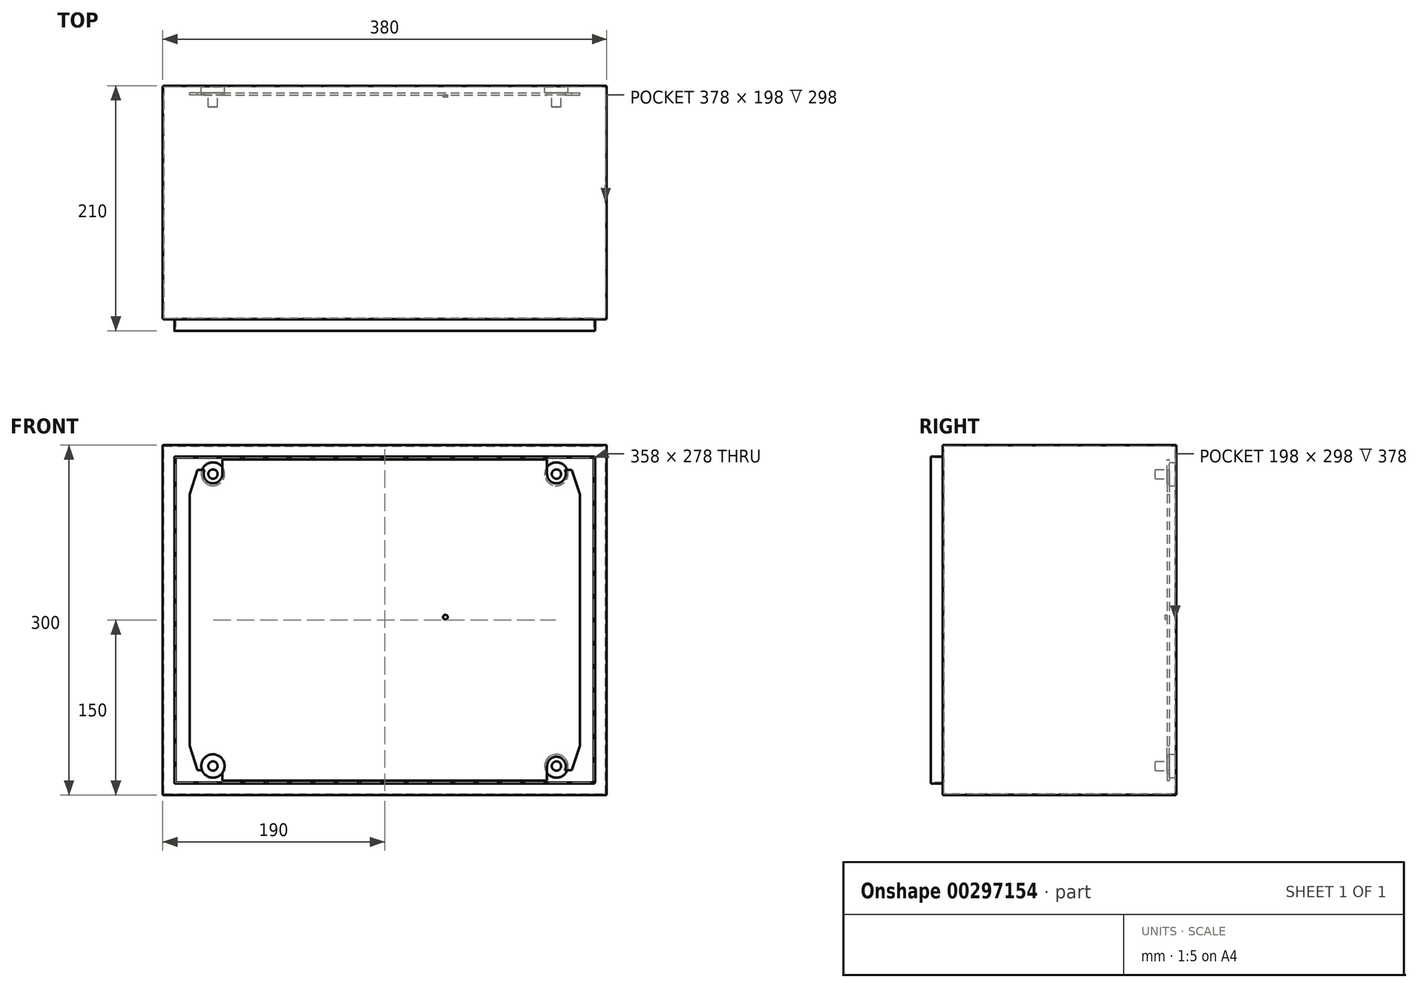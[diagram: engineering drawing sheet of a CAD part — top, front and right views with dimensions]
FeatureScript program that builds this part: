
annotation { "Feature Type Name" : "Feature", "Feature Type Description" : "" }
export const myFeature = defineFeature(function(context is Context, id is Id, definition is map)
    precondition{}
    {
        {
            var Q0;
            Q0=qCreatedBy(makeId("Front.planeOp"),FACE);
            var sketch = newSketch(context, id + "F0", { "sketchPlane" : qUnion([Q0])});
            skLineSegment(sketch, "E0.bottom", {"start": v(190, 150) * mm, "end": v(-190, 150) * mm});
            skLineSegment(sketch, "E0.top", {"start": v(190, -150) * mm, "end": v(-190, -150) * mm});
            skLineSegment(sketch, "E0.left", {"start": v(190, 150) * mm, "end": v(190, -150) * mm});
            skLineSegment(sketch, "E0.right", {"start": v(-190, 150) * mm, "end": v(-190, -150) * mm});
            skPoint(sketch, "E0.middle", {"position": v(0, 0) * mm});
            skSolve(sketch);
        }
        {
            var Q0;
            Q0=makeQuery(id+"F0.imprint","IMPRINT",FACE,{"disambiguationData":[TD([[makeQuery(id+"F0.imprint","IMPRINT",EDGE,{"derivedFrom":sQuery(id+"F0.wireOp",EDGE,"E0.bottom")}),1.0]])]});
            extrude(context, id + "F1", {"entities" : qUnion([Q0]), "depth" : 200 * mm});
        }
        {
            var Q0;
            Q0=makeQuery(id+"F1.opExtrude","CAP_FACE",FACE,{"disambiguationData":[OSD([sQuery(id+"F0.wireOp",EDGE,"E0.bottom"),sQuery(id+"F0.wireOp",EDGE,"E0.top"),sQuery(id+"F0.wireOp",EDGE,"E0.left"),sQuery(id+"F0.wireOp",EDGE,"E0.right")])],"isStart":false});
            var sketch = newSketch(context, id + "F2", { "sketchPlane" : qUnion([Q0])});
            skLineSegment(sketch, "E1.0", {"start": v(190, 150) * mm, "end": v(-190, 150) * mm});
            skLineSegment(sketch, "E1.1", {"start": v(190, 150) * mm, "end": v(190, -150) * mm});
            skLineSegment(sketch, "E1.2", {"start": v(190, -150) * mm, "end": v(-190, -150) * mm});
            skLineSegment(sketch, "E1.3", {"start": v(-190, 150) * mm, "end": v(-190, -150) * mm});
            skLineSegment(sketch, "E2.0", {"start": v(180, 140) * mm, "end": v(-180, 140) * mm});
            skLineSegment(sketch, "E2.1", {"start": v(180, 140) * mm, "end": v(180, -140) * mm});
            skLineSegment(sketch, "E2.2", {"start": v(180, -140) * mm, "end": v(-180, -140) * mm});
            skLineSegment(sketch, "E2.3", {"start": v(-180, 140) * mm, "end": v(-180, -140) * mm});
            skSolve(sketch);
        }
        {
            var Q0;
            Q0=makeQuery(id+"F2.imprint","IMPRINT",FACE,{"disambiguationData":[TD([[makeQuery(id+"F2.imprint","IMPRINT",EDGE,{"derivedFrom":sQuery(id+"F2.wireOp",EDGE,"E2.0")}),1.0]])]});
            extrude(context, id + "F3", {"entities" : qUnion([Q0]), "operationType" : NewBodyOperationType.ADD, "depth" : 10 * mm});
        }
        {
            var Q0;
            Q0=makeQuery(id+"F1.opExtrude","SWEPT_EDGE",EDGE,{"disambiguationData":[OSD([sQuery(id+"F0.wireOp",EDGE,"E0.bottom"),sQuery(id+"F0.wireOp",EDGE,"E0.left")])]});
            var Q1;
            Q1=makeQuery(id+"F1.opExtrude","CAP_EDGE",EDGE,{"disambiguationData":[OSD([sQuery(id+"F0.wireOp",EDGE,"E0.left")])],"isStart":false});
            var Q2;
            Q2=makeQuery(id+"F1.opExtrude","SWEPT_EDGE",EDGE,{"disambiguationData":[OSD([sQuery(id+"F0.wireOp",EDGE,"E0.top"),sQuery(id+"F0.wireOp",EDGE,"E0.left")])]});
            var Q3;
            Q3=makeQuery(id+"F1.opExtrude","CAP_EDGE",EDGE,{"disambiguationData":[OSD([sQuery(id+"F0.wireOp",EDGE,"E0.left")])],"isStart":true});
            var Q4;
            Q4=makeQuery(id+"F1.opExtrude","CAP_EDGE",EDGE,{"disambiguationData":[OSD([sQuery(id+"F0.wireOp",EDGE,"E0.bottom")])],"isStart":false});
            var Q5;
            Q5=makeQuery(id+"F1.opExtrude","SWEPT_EDGE",EDGE,{"disambiguationData":[OSD([sQuery(id+"F0.wireOp",EDGE,"E0.bottom"),sQuery(id+"F0.wireOp",EDGE,"E0.right")])]});
            var Q6;
            Q6=makeQuery(id+"F1.opExtrude","SWEPT_EDGE",EDGE,{"disambiguationData":[OSD([sQuery(id+"F0.wireOp",EDGE,"E0.top"),sQuery(id+"F0.wireOp",EDGE,"E0.right")])]});
            var Q7;
            Q7=makeQuery(id+"F1.opExtrude","CAP_EDGE",EDGE,{"disambiguationData":[OSD([sQuery(id+"F0.wireOp",EDGE,"E0.right")])],"isStart":false});
            var Q8;
            Q8=makeQuery(id+"F1.opExtrude","CAP_EDGE",EDGE,{"disambiguationData":[OSD([sQuery(id+"F0.wireOp",EDGE,"E0.right")])],"isStart":true});
            var Q9;
            Q9=makeQuery(id+"F1.opExtrude","CAP_EDGE",EDGE,{"disambiguationData":[OSD([sQuery(id+"F0.wireOp",EDGE,"E0.bottom")])],"isStart":true});
            var Q10;
            Q10=makeQuery(id+"F1.opExtrude","CAP_EDGE",EDGE,{"disambiguationData":[OSD([sQuery(id+"F0.wireOp",EDGE,"E0.top")])],"isStart":false});
            var Q11;
            Q11=makeQuery(id+"F1.opExtrude","CAP_EDGE",EDGE,{"disambiguationData":[OSD([sQuery(id+"F0.wireOp",EDGE,"E0.top")])],"isStart":true});
            var Q12;
            Q12=makeQuery(id+"F3.opExtrude","SWEPT_EDGE",EDGE,{"disambiguationData":[OSD([sQuery(id+"F2.wireOp",EDGE,"E2.0"),sQuery(id+"F2.wireOp",EDGE,"E2.1")])]});
            var Q13;
            Q13=makeQuery(id+"F3.opExtrude","SWEPT_EDGE",EDGE,{"disambiguationData":[OSD([sQuery(id+"F2.wireOp",EDGE,"E2.0"),sQuery(id+"F2.wireOp",EDGE,"E2.3")])]});
            var Q14;
            Q14=makeQuery(id+"F3.opExtrude","SWEPT_EDGE",EDGE,{"disambiguationData":[OSD([sQuery(id+"F2.wireOp",EDGE,"E2.1"),sQuery(id+"F2.wireOp",EDGE,"E2.2")])]});
            var Q15;
            Q15=makeQuery(id+"F3.opExtrude","SWEPT_EDGE",EDGE,{"disambiguationData":[OSD([sQuery(id+"F2.wireOp",EDGE,"E2.2"),sQuery(id+"F2.wireOp",EDGE,"E2.3")])]});
            fillet(context, id + "F4", {"entities" : qUnion([Q0, Q1, Q2, Q3, Q4, Q5, Q6, Q7, Q8, Q9, Q10, Q11, Q12, Q13, Q14, Q15]), "radius" : 1 * mm, "tangentPropagation" : true, "allowEdgeOverflow" : false});
        }
        {
            var Q0;
            Q0=makeQuery(id+"F3.opExtrude","CAP_FACE",FACE,{"disambiguationData":[OSD([sQuery(id+"F2.wireOp",EDGE,"E2.0"),sQuery(id+"F2.wireOp",EDGE,"E2.1"),sQuery(id+"F2.wireOp",EDGE,"E2.2"),sQuery(id+"F2.wireOp",EDGE,"E2.3")])],"isStart":false});
            shell(context, id + "F5", {"entities" : qUnion([Q0]), "thickness" : 1 * mm});
        }
        {
            var Q0;
            {var subQ0=sQuery(id+"F0.wireOp",EDGE,"E0.right");var subQ1=sQuery(id+"F0.wireOp",EDGE,"E0.left");var subQ2=sQuery(id+"F0.wireOp",EDGE,"E0.top");var subQ3=sQuery(id+"F0.wireOp",EDGE,"E0.bottom");Q0=makeQuery(id+"F5.opShell","OFFSET_FACE",FACE,{"disambiguationData":[OSD([subQ3,subQ2,subQ1,subQ0]),TDD([makeQuery(id+"F1.opExtrude","CAP_FACE",FACE,{"disambiguationData":[OSD([subQ3,subQ2,subQ1,subQ0])],"isStart":true})])]});}
            var sketch = newSketch(context, id + "F6", { "sketchPlane" : qUnion([Q0])});
            skLineSegment(sketch, "E3.bottom", {"start": v(147, -125) * mm, "end": v(-147, -125) * mm, "construction": true});
            skLineSegment(sketch, "E3.top", {"start": v(147, 125) * mm, "end": v(-147, 125) * mm, "construction": true});
            skLineSegment(sketch, "E3.left", {"start": v(147, -125) * mm, "end": v(147, 125) * mm, "construction": true});
            skLineSegment(sketch, "E3.right", {"start": v(-147, -125) * mm, "end": v(-147, 125) * mm, "construction": true});
            skPoint(sketch, "E3.middle", {"position": v(0, 0) * mm});
            skCircle(sketch, "E4", {"center": v(-147, 125) * mm, "radius": 10 * mm});
            skCircle(sketch, "E5.0.1.0", {"center": v(-147, -125) * mm, "radius": 10 * mm});
            skLineSegment(sketch, "E5.direction1", {"start": v(-147, 125) * mm, "end": v(147, 125) * mm, "construction": true});
            skLineSegment(sketch, "E5.direction2", {"start": v(-147, 125) * mm, "end": v(-147, -125) * mm, "construction": true});
            skCircle(sketch, "E6.0.1.0", {"center": v(147, 125) * mm, "radius": 10 * mm});
            skCircle(sketch, "E6.0.1.1", {"center": v(147, -125) * mm, "radius": 10 * mm});
            skCircle(sketch, "E7", {"center": v(-147, 125) * mm, "radius": 4 * mm});
            skCircle(sketch, "E8.0.1.0", {"center": v(-147, -125) * mm, "radius": 4 * mm});
            skCircle(sketch, "E8.1.0.0", {"center": v(147, 125) * mm, "radius": 4 * mm});
            skCircle(sketch, "E8.1.1.0", {"center": v(147, -125) * mm, "radius": 4 * mm});
            skSolve(sketch);
        }
        {
            var Q0;
            Q0=makeQuery(id+"F6.imprint","IMPRINT",FACE,{"disambiguationData":[TD([[makeQuery(id+"F6.imprint","IMPRINT",EDGE,{"derivedFrom":sQuery(id+"F6.wireOp",EDGE,"E5.0.1.0")}),1.0]])]});
            var Q1;
            Q1=makeQuery(id+"F6.imprint","IMPRINT",FACE,{"disambiguationData":[TD([[makeQuery(id+"F6.imprint","IMPRINT",EDGE,{"derivedFrom":sQuery(id+"F6.wireOp",EDGE,"E8.0.1.0")}),1.0]])]});
            var Q2;
            Q2=makeQuery(id+"F6.imprint","IMPRINT",FACE,{"disambiguationData":[TD([[makeQuery(id+"F6.imprint","IMPRINT",EDGE,{"derivedFrom":sQuery(id+"F6.wireOp",EDGE,"E6.0.1.0")}),1.0]])]});
            var Q3;
            Q3=makeQuery(id+"F6.imprint","IMPRINT",FACE,{"disambiguationData":[TD([[makeQuery(id+"F6.imprint","IMPRINT",EDGE,{"derivedFrom":sQuery(id+"F6.wireOp",EDGE,"E8.1.0.0")}),1.0]])]});
            var Q4;
            Q4=makeQuery(id+"F6.imprint","IMPRINT",FACE,{"disambiguationData":[TD([[makeQuery(id+"F6.imprint","IMPRINT",EDGE,{"derivedFrom":sQuery(id+"F6.wireOp",EDGE,"E4")}),1.0]])]});
            var Q5;
            Q5=makeQuery(id+"F6.imprint","IMPRINT",FACE,{"disambiguationData":[TD([[makeQuery(id+"F6.imprint","IMPRINT",EDGE,{"derivedFrom":sQuery(id+"F6.wireOp",EDGE,"E7")}),1.0]])]});
            var Q6;
            Q6=makeQuery(id+"F6.imprint","IMPRINT",FACE,{"disambiguationData":[TD([[makeQuery(id+"F6.imprint","IMPRINT",EDGE,{"derivedFrom":sQuery(id+"F6.wireOp",EDGE,"E6.0.1.1")}),1.0]])]});
            var Q7;
            Q7=makeQuery(id+"F6.imprint","IMPRINT",FACE,{"disambiguationData":[TD([[makeQuery(id+"F6.imprint","IMPRINT",EDGE,{"derivedFrom":sQuery(id+"F6.wireOp",EDGE,"E8.1.1.0")}),1.0]])]});
            extrude(context, id + "F7", {"entities" : qUnion([Q0, Q1, Q2, Q3, Q4, Q5, Q6, Q7]), "operationType" : NewBodyOperationType.ADD, "depth" : 5 * mm});
        }
        {
            var Q0;
            Q0=makeQuery(id+"F7.opExtrude","CAP_FACE",FACE,{"disambiguationData":[OSD([sQuery(id+"F6.wireOp",EDGE,"E4")])],"isStart":false});
            var sketch = newSketch(context, id + "F8", { "sketchPlane" : qUnion([Q0])});
            skCircle(sketch, "E9.0", {"center": v(-147, 125) * mm, "radius": 4 * mm});
            skCircle(sketch, "E9.1", {"center": v(147, 125) * mm, "radius": 4 * mm});
            skCircle(sketch, "E9.2", {"center": v(147, -125) * mm, "radius": 4 * mm});
            skCircle(sketch, "E9.3", {"center": v(-147, -125) * mm, "radius": 4 * mm});
            skSolve(sketch);
        }
        {
            var Q0;
            Q0=makeQuery(id+"F8.imprint","IMPRINT",FACE,{"disambiguationData":[TD([[makeQuery(id+"F8.imprint","IMPRINT",EDGE,{"derivedFrom":sQuery(id+"F8.wireOp",EDGE,"E9.0")}),1.0]])]});
            var Q1;
            Q1=makeQuery(id+"F8.imprint","IMPRINT",FACE,{"disambiguationData":[TD([[makeQuery(id+"F8.imprint","IMPRINT",EDGE,{"derivedFrom":sQuery(id+"F8.wireOp",EDGE,"E9.1")}),1.0]])]});
            var Q2;
            Q2=makeQuery(id+"F8.imprint","IMPRINT",FACE,{"disambiguationData":[TD([[makeQuery(id+"F8.imprint","IMPRINT",EDGE,{"derivedFrom":sQuery(id+"F8.wireOp",EDGE,"E9.3")}),1.0]])]});
            var Q3;
            Q3=makeQuery(id+"F8.imprint","IMPRINT",FACE,{"disambiguationData":[TD([[makeQuery(id+"F8.imprint","IMPRINT",EDGE,{"derivedFrom":sQuery(id+"F8.wireOp",EDGE,"E9.2")}),1.0]])]});
            extrude(context, id + "F9", {"entities" : qUnion([Q0, Q1, Q2, Q3]), "operationType" : NewBodyOperationType.ADD, "depth" : 12 * mm});
        }
        {
            var Q0;
            Q0=makeQuery(id+"F7.opExtrude","CAP_FACE",FACE,{"disambiguationData":[OSD([sQuery(id+"F6.wireOp",EDGE,"E5.0.1.0")])],"isStart":false});
            var sketch = newSketch(context, id + "F10", { "sketchPlane" : qUnion([Q0])});
            skLineSegment(sketch, "E10.bottom", {"start": v(139, 137.5) * mm, "end": v(-139, 137.5) * mm});
            skLineSegment(sketch, "E10.top", {"start": v(139, -137.5) * mm, "end": v(-137, -137.5) * mm});
            skLineSegment(sketch, "E10.left", {"start": v(167, 107.5) * mm, "end": v(167, -107.5) * mm});
            skLineSegment(sketch, "E10.right", {"start": v(-167, 107.5) * mm, "end": v(-167, -107.5) * mm});
            skPoint(sketch, "E10.middle", {"position": v(0, 0) * mm});
            skArc(sketch, "E11", {"start": v(-154.2, 128.5) * mm, "mid": v(-147, 117) * mm, "end": v(-139.8, 128.5) * mm});
            skArc(sketch, "E12.0.1.0", {"start": v(-139, -125) * mm, "mid": v(-148.8, -117.2) * mm, "end": v(-154.2, -128.5) * mm});
            skArc(sketch, "E12.1.0.0", {"start": v(139, 125) * mm, "mid": v(148.8, 117.2) * mm, "end": v(154.2, 128.5) * mm});
            skArc(sketch, "E12.1.1.0", {"start": v(154.2, -128.5) * mm, "mid": v(148.8, -117.2) * mm, "end": v(139, -125) * mm});
            skLineSegment(sketch, "E12.direction1", {"start": v(-147, 125) * mm, "end": v(-139, 125) * mm, "construction": true});
            skLineSegment(sketch, "E13", {"start": v(-139, 125) * mm, "end": v(-139, 137.5) * mm});
            skLineSegment(sketch, "E14", {"start": v(139, 125) * mm, "end": v(139, 137.5) * mm});
            skLineSegment(sketch, "E15.trimOffspring", {"start": v(139, 125) * mm, "end": v(147, 125) * mm, "construction": true});
            skPoint(sketch, "E16.orphan", {"position": v(-167, 137.5) * mm});
            skPoint(sketch, "E17.orphan", {"position": v(167, 137.5) * mm});
            skPoint(sketch, "E18.orphan", {"position": v(-167, -137.5) * mm});
            skLineSegment(sketch, "E19", {"start": v(139, -125) * mm, "end": v(139, -137.5) * mm});
            skLineSegment(sketch, "E20", {"start": v(-139, -125) * mm, "end": v(-139, -137.5) * mm});
            skLineSegment(sketch, "E21", {"start": v(-139, -137.5) * mm, "end": v(-137, -137.5) * mm});
            skLineSegment(sketch, "E22", {"start": v(154.2, -128.5) * mm, "end": v(160.2, -128.5) * mm});
            skLineSegment(sketch, "E23", {"start": v(160.2, -128.5) * mm, "end": v(167, -107.5) * mm});
            skPoint(sketch, "E24.orphan", {"position": v(167, -137.5) * mm});
            skLineSegment(sketch, "E25", {"start": v(-154.2, -128.5) * mm, "end": v(-160.2, -128.5) * mm});
            skLineSegment(sketch, "E26", {"start": v(-160.2, -128.5) * mm, "end": v(-167, -107.5) * mm});
            skLineSegment(sketch, "E27", {"start": v(-154.2, 128.5) * mm, "end": v(-160.2, 128.5) * mm});
            skLineSegment(sketch, "E28", {"start": v(-160.2, 128.5) * mm, "end": v(-167, 107.5) * mm});
            skLineSegment(sketch, "E29", {"start": v(154.2, 128.5) * mm, "end": v(160.2, 128.5) * mm});
            skLineSegment(sketch, "E30", {"start": v(160.2, 128.5) * mm, "end": v(167, 107.5) * mm});
            skSolve(sketch);
        }
        {
            var Q0;
            Q0=makeQuery(id+"F10.imprint","IMPRINT",FACE,{"disambiguationData":[TD([[makeQuery(id+"F10.imprint","IMPRINT",EDGE,{"derivedFrom":sQuery(id+"F10.wireOp",EDGE,"E10.bottom")}),1.0]])]});
            extrude(context, id + "F11", {"entities" : qUnion([Q0]), "depth" : 2 * mm});
        }
        {
            var Q0;
            Q0=makeQuery(id+"F11.opExtrude","CAP_FACE",FACE,{"disambiguationData":[OSD([sQuery(id+"F6.wireOp",EDGE,"E5.0.1.0"),sQuery(id+"F10.wireOp",EDGE,"E10.bottom"),sQuery(id+"F10.wireOp",EDGE,"E10.top"),sQuery(id+"F10.wireOp",EDGE,"E10.left"),sQuery(id+"F10.wireOp",EDGE,"E10.right"),sQuery(id+"F10.wireOp",EDGE,"E11"),sQuery(id+"F10.wireOp",EDGE,"E12.1.0.0"),sQuery(id+"F10.wireOp",EDGE,"E12.1.1.0"),sQuery(id+"F10.wireOp",EDGE,"E13"),sQuery(id+"F10.wireOp",EDGE,"E14"),sQuery(id+"F10.wireOp",EDGE,"E19"),sQuery(id+"F10.wireOp",EDGE,"E20"),sQuery(id+"F10.wireOp",EDGE,"E21"),sQuery(id+"F10.wireOp",EDGE,"E22"),sQuery(id+"F10.wireOp",EDGE,"E23"),sQuery(id+"F10.wireOp",EDGE,"E25"),sQuery(id+"F10.wireOp",EDGE,"E26"),sQuery(id+"F10.wireOp",EDGE,"E27"),sQuery(id+"F10.wireOp",EDGE,"E28"),sQuery(id+"F10.wireOp",EDGE,"E29"),sQuery(id+"F10.wireOp",EDGE,"E30")])],"isStart":false});
            var sketch = newSketch(context, id + "F12", { "sketchPlane" : qUnion([Q0])});
            skLineSegment(sketch, "E31.0", {"start": v(162, 107.5) * mm, "end": v(162, -107.5) * mm, "construction": true});
            skLineSegment(sketch, "E32.0", {"start": v(-162, 107.5) * mm, "end": v(-162, -107.5) * mm, "construction": true});
            skLineSegment(sketch, "E33", {"start": v(-167, 2.5) * mm, "end": v(167, 2.5) * mm, "construction": true});
            skCircle(sketch, "E34", {"center": v(52, 2.5) * mm, "radius": 2 * mm});
            skSolve(sketch);
        }
        {
            var Q0;
            Q0=makeQuery(id+"F12.imprint","IMPRINT",FACE,{"disambiguationData":[TD([[makeQuery(id+"F12.imprint","IMPRINT",EDGE,{"derivedFrom":sQuery(id+"F12.wireOp",EDGE,"E34")}),1.0]])]});
            extrude(context, id + "F13", {"entities" : qUnion([Q0]), "operationType" : NewBodyOperationType.ADD, "depth" : 1.5 * mm});
        }
    });
